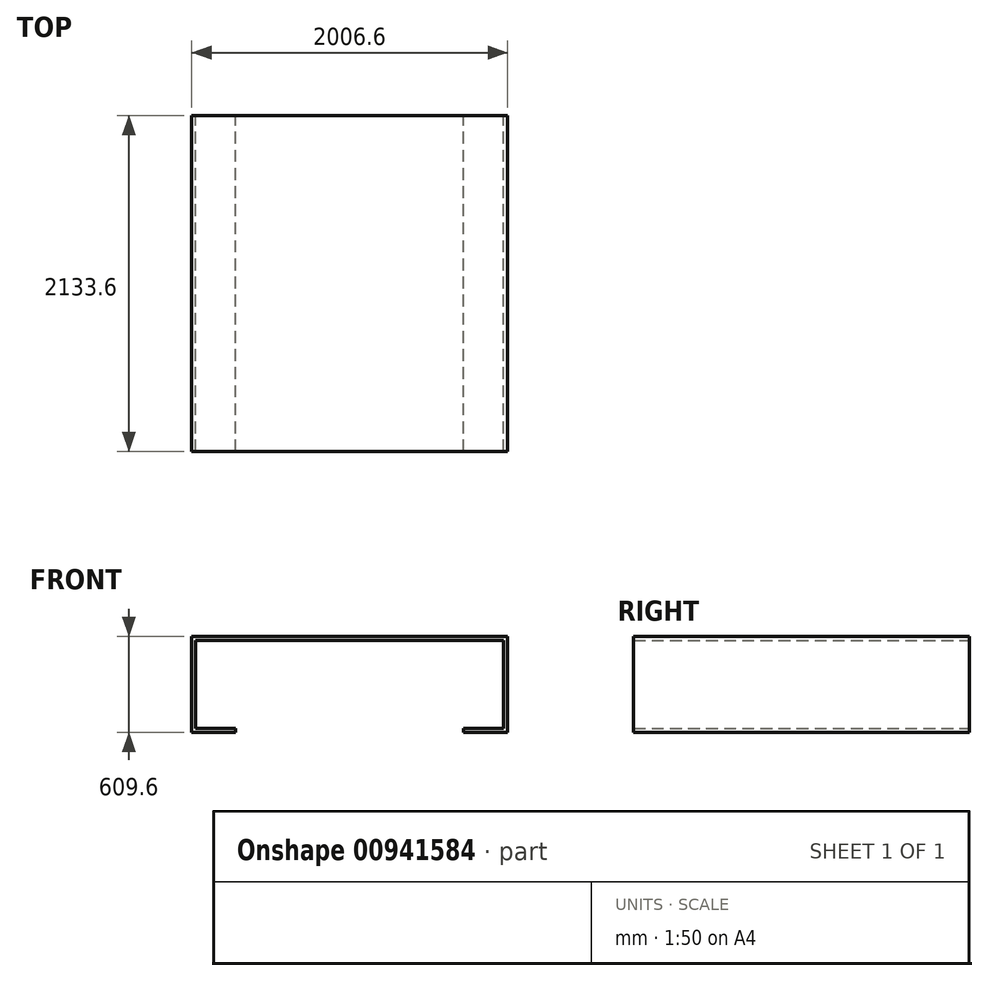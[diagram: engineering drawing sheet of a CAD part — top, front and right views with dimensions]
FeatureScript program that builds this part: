
annotation { "Feature Type Name" : "Feature", "Feature Type Description" : "" }
export const myFeature = defineFeature(function(context is Context, id is Id, definition is map)
    precondition{}
    {
        {
            var Q0;
            Q0=qCreatedBy(makeId("Front.planeOp"),FACE);
            var sketch = newSketch(context, id + "F0", { "sketchPlane" : qUnion([Q0])});
            skLineSegment(sketch, "E0", {"start": v(0, 0) * mm, "end": v(-254, 0) * mm});
            skLineSegment(sketch, "E1", {"start": v(-254, 0) * mm, "end": v(-254, 558.8) * mm});
            skLineSegment(sketch, "E2", {"start": v(-254, 558.8) * mm, "end": v(1701.8, 558.8) * mm});
            skLineSegment(sketch, "E3", {"start": v(1701.8, 558.8) * mm, "end": v(1701.8, 0) * mm});
            skLineSegment(sketch, "E4", {"start": v(1701.8, 0) * mm, "end": v(1447.8, 0) * mm});
            skLineSegment(sketch, "E5", {"start": v(1447.8, 0) * mm, "end": v(1447.8, -25.4) * mm});
            skLineSegment(sketch, "E6", {"start": v(1447.8, -25.4) * mm, "end": v(1727.2, -25.4) * mm});
            skLineSegment(sketch, "E7", {"start": v(1727.2, -25.4) * mm, "end": v(1727.2, 584.2) * mm});
            skLineSegment(sketch, "E8", {"start": v(1727.2, 584.2) * mm, "end": v(-279.4, 584.2) * mm});
            skLineSegment(sketch, "E9", {"start": v(-279.4, 584.2) * mm, "end": v(-279.4, -25.4) * mm});
            skLineSegment(sketch, "E10", {"start": v(-279.4, -25.4) * mm, "end": v(0, -25.4) * mm});
            skLineSegment(sketch, "E11", {"start": v(0, -25.4) * mm, "end": v(0, 0) * mm});
            skSolve(sketch);
        }
        {
            var Q0;
            Q0 = qSketchRegion(id + "F0", true);
            extrude(context, id + "F1", {"entities" : qUnion([Q0]), "depth" : 2133.6 * mm, "offsetDistance" : 25.4 * mm});
        }
    });
